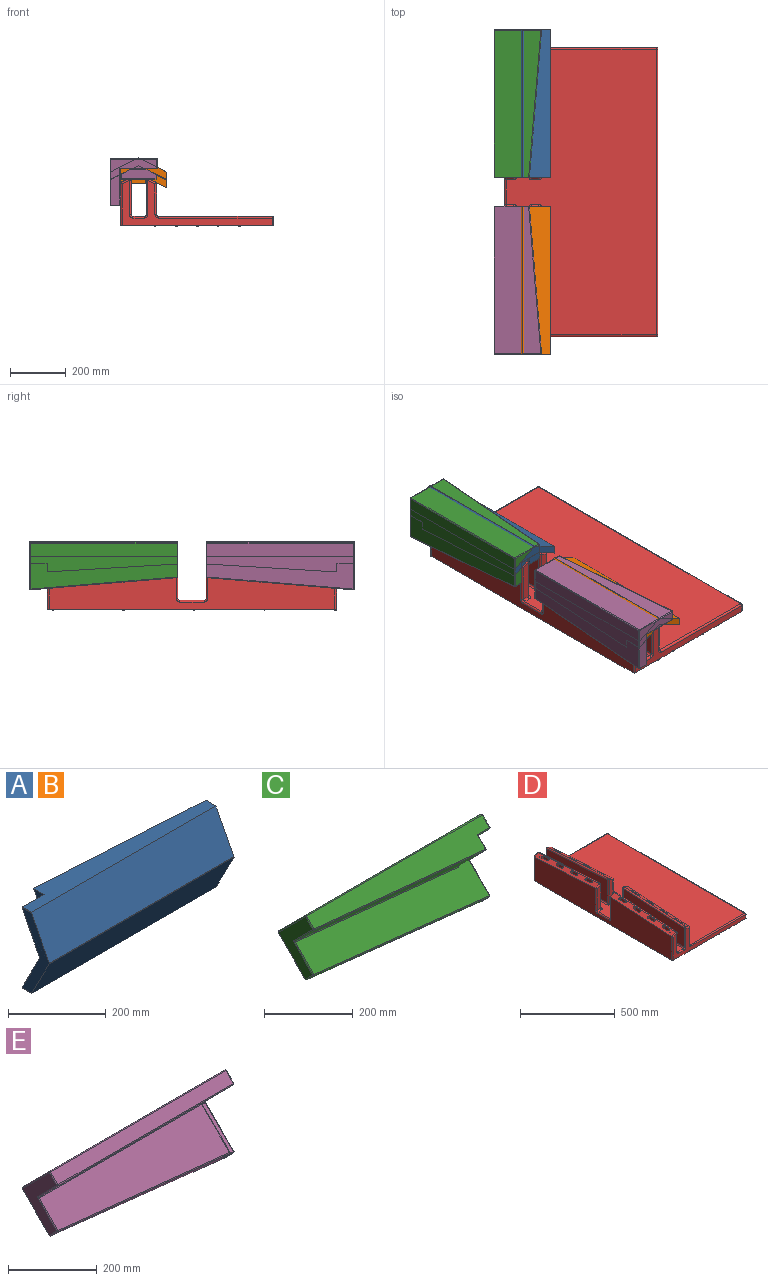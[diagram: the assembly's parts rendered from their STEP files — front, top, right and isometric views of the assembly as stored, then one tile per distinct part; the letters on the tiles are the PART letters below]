
ASSEMBLY  parts=5 mates=8
PART A: 33 faces, bbox 534.4x110.4x204.2 mm
  f0: plane 469.9x75.61mm, normal (0.05,0.89,0.46), area 39897.8mm2, adj f1,f2,f6,f23
  f1: plane 532.14x57.13mm, normal (0,0,-1), area 21788.8mm2, adj f0,f6,f10,f11,f14,f23,f31
  f2: plane 469.9x52.97mm, normal (0,0.02,-1), area 11550.8mm2, adj f0,f6,f15,f23
  f3: plane 469.9x52.97mm, normal (0,0.02,1), area 11550.8mm2, adj f4,f6,f15,f23
  f4: plane 469.9x75.61mm, normal (0.05,0.89,-0.46), area 39897.8mm2, adj f3,f5,f6,f23
  f5: plane 532.14x57.13mm, normal (0,0,1), area 21788.8mm2, adj f4,f6,f8,f9,f16,f23,f32
  f6: plane 203.66x79.94mm, normal (-1,0,0), area 7130.9mm2, adj f0,f1,f2,f3,f4,f5,f9,f10
  f7: sphere r=1.27mm, area 2.2mm2, adj f8,f16,f20
  f8: cylinder r=1.27mm len=60.96mm, axis (-1,0,0), area 158.5mm2, adj f5,f7,f9,f13
  f9: bspline ~2.87x2.62mm, area 4.1mm2, adj f5,f6,f8,f21
  f10: bspline ~2.76x2.54mm, area 4.1mm2, adj f1,f6,f11,f22
  f11: cylinder r=1.27mm len=60.96mm, axis (-1,0,0), area 158.5mm2, adj f1,f10,f12,f18
  f12: sphere r=1.27mm, area 2.2mm2, adj f11,f14,f17
  f13: plane 99.17x62.23mm, normal (0,0.89,-0.46), area 6866mm2, adj f8,f19,f20,f21,f27
  f14: cylinder r=1.27mm len=26.49mm, axis (0,-1,0), area 52.8mm2, adj f1,f12,f19,f29
  f15: plane 469.9x52.11mm, normal (0.06,1,0), area 24298.6mm2, adj f2,f3,f6,f23
  f16: cylinder r=1.27mm len=26.49mm, axis (0,1,0), area 52.8mm2, adj f5,f7,f19,f26
  f17: cylinder r=1.27mm len=54.17mm, axis (0,-0.46,0.89), area 117.8mm2, adj f12,f18,f19,f28
  f18: plane 99.17x62.23mm, normal (0,0.89,0.46), area 6865.9mm2, adj f11,f17,f19,f22,f27,f28
  f19: plane 203.2x78.7mm, normal (-1,0,0), area 5581.4mm2, adj f13,f14,f16,f17,f18,f20,f25,f26
  f20: cylinder r=1.27mm len=54.14mm, axis (0,-0.46,-0.89), area 118.8mm2, adj f7,f13,f19,f25
  f21: cylinder r=1.27mm len=100.91mm, axis (0,0.46,0.89), area 223.5mm2, adj f6,f9,f13,f24
  f22: cylinder r=1.27mm len=100.91mm, axis (0,0.46,-0.89), area 223.5mm2, adj f6,f10,f18,f24
  f23: plane 203.2x80.81mm, normal (1,0,0), area 7457.9mm2, adj f0,f1,f2,f3,f4,f5,f15,f30
  f24: sphere r=1.27mm, area 1.4mm2, adj f21,f22,f27
  f25: plane 3.07x0.99mm, normal (0,1,0), area 0.4mm2, adj f19,f20
  f26: plane 1.27x1.27mm, normal (0,1,0), area 0.3mm2, adj f16,f19,f32
  f27: cylinder r=1.27mm len=62.23mm, axis (-1,0,0), area 75.2mm2, adj f13,f18,f19,f24
  f28: plane 3.81x2.31mm, normal (0,1,0), area 0.8mm2, adj f17,f18,f19
  f29: plane 1.27x1.27mm, normal (0,1,0), area 0.3mm2, adj f14,f19,f31
  f30: cylinder r=1.27mm len=533.4mm, axis (-1,0,0), area 644.7mm2, adj f19,f23,f31,f32
  f31: plane 533.4x101.02mm, normal (0,-0.89,-0.46), area 60618.5mm2, adj f1,f19,f23,f29,f30
  f32: plane 533.4x101.02mm, normal (0,-0.89,0.46), area 60618.5mm2, adj f5,f19,f23,f26,f30
PART B: same geometry as A
PART C: 56 faces, bbox 533.4x170.4x240.4 mm
  f0: cylinder r=2.54mm len=0.77mm, axis (0,-0.71,-0.71), area 0.1mm2, adj f6,f27,f42
  f1: cylinder r=2.54mm len=37.24mm, axis (1,-0.06,0.06), area 138.1mm2, adj f11,f12,f18,f55
  f2: cylinder r=2.54mm len=528.58mm, axis (-1,0.06,0.06), area 2115.4mm2, adj f5,f10,f21,f32
  f3: cylinder r=2.54mm len=528.58mm, axis (1,-0.06,0.06), area 2115.4mm2, adj f7,f12,f22,f31
  f4: cylinder r=2.54mm len=528.37mm, axis (1,0,0), area 2108.1mm2, adj f7,f10,f25,f35
  f5: plane 528.37x54.49mm, normal (-0.08,-0.7,-0.71), area 17507.3mm2, adj f2,f14,f19,f30
  f6: plane 172.76x109.95mm, normal (-1,0,0), area 7001.3mm2, adj f0,f26,f27,f28,f29,f30,f31,f32
  f7: plane 528.37x117.66mm, normal (0,0.71,0.71), area 76157.4mm2, adj f3,f4,f24,f33
  f8: plane 235.02x141.02mm, normal (1,0,0), area 9899.2mm2, adj f15,f16,f17,f18,f19,f20,f21,f22
  f9: plane 528.37x90.7mm, normal (0,-0.71,0.71), area 46551.3mm2, adj f14,f15,f26,f36,f49,f50,f51
  f10: plane 528.37x117.66mm, normal (0,0.71,-0.71), area 76157.4mm2, adj f2,f4,f23,f34
  f11: plane 90.7x90.43mm, normal (0,-0.71,-0.71), area 4049.6mm2, adj f1,f16,f36,f53,f54
  f12: plane 528.37x78.86mm, normal (-0.08,-0.71,0.7), area 26822.7mm2, adj f1,f3,f13,f20,f29,f40,f41,f46
  f13: cylinder r=2.54mm len=0.02mm, axis (1,-0.06,0.06), area 0mm2, adj f12,f27,f40
  f14: cylinder r=2.54mm len=528.58mm, axis (1,-0.06,-0.06), area 2115.4mm2, adj f5,f9,f17,f28
  f15: cylinder r=2.51mm len=96.03mm, axis (0,0.71,0.71), area 515.8mm2, adj f8,f9,f17,f37
  f16: cylinder r=2.51mm len=96.03mm, axis (0,0.71,-0.71), area 515.8mm2, adj f8,f11,f18,f37
  f17: bspline ~3.75x2.72mm, area 10.6mm2, adj f8,f14,f15,f19
  f18: bspline ~3.75x2.72mm, area 10.6mm2, adj f1,f8,f16,f20
  f19: cylinder r=2.51mm len=25.16mm, axis (0,-0.71,0.71), area 137.3mm2, adj f5,f8,f17,f21
  f20: cylinder r=2.51mm len=25.16mm, axis (0,0.71,0.71), area 137.3mm2, adj f8,f12,f18,f22
  f21: bspline ~3.75x2.72mm, area 10.6mm2, adj f2,f8,f19,f23
  f22: bspline ~3.75x2.72mm, area 10.6mm2, adj f3,f8,f20,f24
  f23: cylinder r=2.51mm len=119.43mm, axis (0,-0.71,-0.71), area 656.3mm2, adj f8,f10,f21,f25
  f24: cylinder r=2.51mm len=119.43mm, axis (0,0.71,-0.71), area 656.3mm2, adj f7,f8,f22,f25
  f25: torus R=0.03mm, axis (1,0,0), area 10.1mm2, adj f4,f8,f23,f24
  f26: cylinder r=2.51mm len=64.74mm, axis (0,0.71,0.71), area 338.5mm2, adj f6,f9,f28,f47,f48
  f27: bspline ~3.43x2.5mm, area 0.6mm2, adj f0,f6,f13,f29,f40,f42
  f28: bspline ~3.59x2.51mm, area 9.5mm2, adj f6,f14,f26,f30
  f29: cylinder r=2.51mm len=25.15mm, axis (0,-0.71,-0.71), area 123.5mm2, adj f6,f12,f27,f31
  f30: cylinder r=2.51mm len=25.15mm, axis (0,0.71,-0.71), area 123.5mm2, adj f5,f6,f28,f32
  f31: bspline ~3.59x2.75mm, area 9.5mm2, adj f3,f6,f29,f33
  f32: bspline ~3.59x2.75mm, area 9.5mm2, adj f2,f6,f30,f34
  f33: cylinder r=2.51mm len=88.25mm, axis (0,0.71,-0.71), area 482.4mm2, adj f6,f7,f31,f35
  f34: cylinder r=2.51mm len=88.25mm, axis (0,-0.71,-0.71), area 482.4mm2, adj f6,f10,f32,f35
  f35: torus R=0.03mm, axis (-1,0,0), area 10.1mm2, adj f4,f6,f33,f34
  f36: cylinder r=2.51mm len=31.95mm, axis (-1,0,0), area 126.2mm2, adj f9,f11,f37,f52
  f37: bspline ~5.34x3.56mm, area 6.7mm2, adj f15,f16,f36
  f38: plane 491.32x114.92mm, normal (-0.08,-0.7,-0.71), area 51488.3mm2, adj f41,f43,f44,f48,f49
  f39: plane 111.46x111.27mm, normal (1,0,0), area 4064.3mm2, adj f44,f46,f51,f53
  f40: cylinder r=2.54mm len=0.93mm, axis (0,-0.71,-0.71), area 0.1mm2, adj f12,f13,f27,f42
  f41: cylinder r=2.54mm len=491.41mm, axis (-0.99,0.11,0), area 1964.8mm2, adj f12,f38,f42,f45
  f42: sphere r=2.54mm, area 9mm2, adj f0,f27,f40,f41,f43
  f43: cylinder r=2.54mm len=64.87mm, axis (0,0.71,-0.71), area 328.6mm2, adj f6,f38,f42,f47
  f44: cylinder r=2.54mm len=90.29mm, axis (0,-0.71,0.71), area 522.7mm2, adj f38,f39,f45,f50
  f45: sphere r=2.54mm, area 11.2mm2, adj f41,f44,f46
  f46: cylinder r=2.54mm len=28.42mm, axis (0,-0.71,-0.71), area 144mm2, adj f12,f39,f45,f54,f55
  f47: bspline ~5.36x3.58mm, area 7mm2, adj f26,f43,f48
  f48: bspline ~3.6x0.73mm, area 1mm2, adj f26,f38,f47,f49
  f49: cylinder r=2.54mm len=491.15mm, axis (-1,0.05,0.05), area 1964.5mm2, adj f9,f38,f48,f50
  f50: torus R=5.08mm, axis (0,0.71,-0.71), area 22.8mm2, adj f9,f44,f49,f51
  f51: cylinder r=2.54mm len=24.84mm, axis (0,-0.71,-0.71), area 129.8mm2, adj f9,f39,f50,f52
  f52: bspline ~3.56x2.54mm, area 7.1mm2, adj f36,f51,f53
  f53: cylinder r=2.54mm len=90.3mm, axis (0,0.71,-0.71), area 498.6mm2, adj f11,f39,f52,f54
  f54: torus R=5.08mm, axis (0,-0.71,-0.71), area 1.1mm2, adj f11,f46,f53,f55
  f55: bspline ~5.27x5.24mm, area 6.8mm2, adj f1,f46,f54
PART D: 236 faces, bbox 552.9x1041.8x201.4 mm
  f0: plane 1041.4x552.45mm, normal (0,0,-1), area 560077.8mm2, adj f4,f6,f7,f16,f17,f52,f53,f54
  f1: plane 1028.7x539.75mm, normal (0,0,1), area 468237mm2, adj f14,f15,f24,f25,f28,f32,f33,f39
  f2: plane 151.7x25.4mm, normal (0,1,0), area 3686.9mm2, adj f34,f35,f43,f44
  f3: plane 151.7x25.4mm, normal (0,1,0), area 3686.9mm2, adj f12,f13,f23,f24
  f4: plane 539.75x162.05mm, normal (0,-1,0), area 20422.9mm2, adj f0,f16,f17,f21,f25,f26,f29,f30
  f5: plane 457.2x142.48mm, normal (1,0,0), area 58803.4mm2, adj f11,f26,f33,f34,f35
  f6: plane 1028.7x25.4mm, normal (1,0,0), area 26129mm2, adj f0,f15,f16,f118
  f7: plane 1028.7x180.58mm, normal (-1,0,0), area 155417.8mm2, adj f0,f10,f12,f13,f14,f17,f19,f114
  f8: plane 457.2x151.7mm, normal (-1,0,0), area 63013.9mm2, adj f36,f41,f44,f47
  f9: plane 457.2x151.7mm, normal (1,0,0), area 63013.9mm2, adj f22,f23,f31,f32
  f10: plane 457.65x43.06mm, normal (-0.46,-0.05,0.89), area 12093.9mm2, adj f7,f12,f17,f21,f22,f50,f68,f69
  f11: plane 457.65x43.06mm, normal (0.46,-0.05,0.89), area 12093.9mm2, adj f5,f26,f30,f35,f36,f48,f52,f53
  f12: cylinder r=6.35mm len=31.75mm, axis (0.89,0,0.46), area 320.7mm2, adj f3,f7,f10,f13,f18
  f13: cylinder r=6.35mm len=142.48mm, axis (0,0,1), area 1407.1mm2, adj f3,f7,f12,f19
  f14: cylinder r=6.35mm len=88.9mm, axis (0,1,0), area 886.7mm2, adj f1,f7,f19,f121
  f15: cylinder r=6.35mm len=1028.7mm, axis (0,-1,0), area 10260.8mm2, adj f1,f6,f20,f122
  f16: cylinder r=6.35mm len=25.4mm, axis (0,0,-1), area 253.4mm2, adj f0,f4,f6,f20
  f17: cylinder r=6.35mm len=152.84mm, axis (0,0,1), area 1510.4mm2, adj f0,f4,f7,f10,f21
  f18: sphere r=6.35mm, area 86.1mm2, adj f12,f22,f23
  f19: torus R=12.7mm, axis (-1,0,0), area 135.6mm2, adj f7,f13,f14,f24
  f20: sphere r=6.35mm, area 63.3mm2, adj f15,f16,f25
  f21: cylinder r=6.35mm len=31.74mm, axis (0.89,0,0.46), area 298.5mm2, adj f4,f10,f17,f27
  f22: cylinder r=6.35mm len=457.58mm, axis (0,-1,-0.06), area 5950.7mm2, adj f9,f10,f18,f27
  f23: cylinder r=6.35mm len=151.7mm, axis (0,0,-1), area 1513.1mm2, adj f3,f9,f18,f28
  f24: cylinder r=6.35mm len=25.4mm, axis (-1,0,0), area 253.4mm2, adj f1,f3,f19,f28
  f25: cylinder r=6.35mm len=409.58mm, axis (-1,0,0), area 4085.3mm2, adj f1,f4,f20,f29
  f26: cylinder r=6.35mm len=114.74mm, axis (0,0,-1), area 1130.4mm2, adj f4,f5,f11,f29,f30
  f27: sphere r=6.35mm, area 79mm2, adj f21,f22,f31
  f28: torus R=12.7mm, axis (0,0,-1), area 135.6mm2, adj f1,f23,f24,f32
  f29: torus R=12.7mm, axis (0,1,0), area 135.6mm2, adj f4,f25,f26,f33
  f30: cylinder r=6.35mm len=31.74mm, axis (0.89,0,-0.46), area 298.5mm2, adj f4,f11,f26,f37
  f31: cylinder r=6.35mm len=123.95mm, axis (0,0,-1), area 1236.4mm2, adj f4,f9,f27,f38
  f32: cylinder r=6.35mm len=457.2mm, axis (0,-1,0), area 4560.4mm2, adj f1,f9,f28,f38
  f33: cylinder r=6.35mm len=457.2mm, axis (0,1,0), area 4560.4mm2, adj f1,f5,f29,f39
  f34: cylinder r=6.35mm len=142.48mm, axis (0,0,-1), area 1407.1mm2, adj f2,f5,f35,f39
  f35: cylinder r=6.35mm len=31.75mm, axis (0.89,0,-0.46), area 320.7mm2, adj f2,f5,f11,f34,f40
  f36: cylinder r=6.35mm len=457.58mm, axis (0,1,0.06), area 5950.7mm2, adj f8,f11,f37,f40
  f37: sphere r=6.35mm, area 79mm2, adj f30,f36,f41
  f38: torus R=12.7mm, axis (0,1,0), area 135.6mm2, adj f4,f31,f32,f42
  f39: torus R=12.7mm, axis (0,0,-1), area 135.6mm2, adj f1,f33,f34,f43
  f40: sphere r=6.35mm, area 86.1mm2, adj f35,f36,f44
  f41: cylinder r=6.35mm len=123.95mm, axis (0,0,1), area 1236.4mm2, adj f4,f8,f37,f45
  f42: cylinder r=6.35mm len=41.28mm, axis (1,0,0), area 411.7mm2, adj f1,f4,f38,f45
  f43: cylinder r=6.35mm len=25.4mm, axis (-1,0,0), area 253.4mm2, adj f1,f2,f39,f46
  f44: cylinder r=6.35mm len=151.7mm, axis (0,0,1), area 1513.1mm2, adj f2,f8,f40,f46
  f45: torus R=12.7mm, axis (0,1,0), area 135.6mm2, adj f4,f41,f42,f47
  f46: torus R=12.7mm, axis (0,0,-1), area 135.6mm2, adj f1,f43,f44,f47
  f47: cylinder r=6.35mm len=457.2mm, axis (0,-1,0), area 4560.4mm2, adj f1,f8,f45,f46
  f48: cylinder r=1.9mm len=17.85mm, axis (0,0,1), area 200.7mm2, adj f11,f49
  f49: cone r=0mm half-angle=59deg, axis (0,0,1), area 13.2mm2, adj f48
  f50: cylinder r=1.9mm len=17.85mm, axis (0,0,1), area 200.7mm2, adj f10,f51
  f51: cone r=0mm half-angle=59deg, axis (0,0,1), area 13.2mm2, adj f50
  f52: cylinder r=6.35mm len=167mm, axis (0,0,1), area 3261.2mm2, adj f0,f11,f53,f55
  f53: plane 162.76x38.1mm, normal (-1,0,0), area 6157.2mm2, adj f0,f11,f52,f54
  f54: cylinder r=6.35mm len=169.34mm, axis (0,0,1), area 3317.1mm2, adj f0,f11,f53,f55
  f55: plane 169.31x38.1mm, normal (1,0,0), area 6406.6mm2, adj f0,f11,f52,f54
  f56: cylinder r=6.35mm len=186.65mm, axis (0,0,1), area 3653.3mm2, adj f0,f11,f57,f59
  f57: plane 182.42x38.1mm, normal (-1,0,0), area 6906mm2, adj f0,f11,f56,f58
  f58: cylinder r=6.35mm len=188.99mm, axis (0,0,1), area 3709.2mm2, adj f0,f11,f57,f59
  f59: plane 188.96x38.1mm, normal (1,0,0), area 7155.4mm2, adj f0,f11,f56,f58
  f60: cylinder r=6.35mm len=180.1mm, axis (0,0,1), area 3522.6mm2, adj f0,f11,f61,f63
  f61: plane 175.86x38.1mm, normal (-1,0,0), area 6656.4mm2, adj f0,f11,f60,f62
  f62: cylinder r=6.35mm len=182.44mm, axis (0,0,1), area 3578.5mm2, adj f0,f11,f61,f63
  f63: plane 182.41x38.1mm, normal (1,0,0), area 6905.8mm2, adj f0,f11,f60,f62
  f64: cylinder r=6.35mm len=173.55mm, axis (0,0,1), area 3391.9mm2, adj f0,f11,f65,f67
  f65: plane 169.31x38.1mm, normal (-1,0,0), area 6406.8mm2, adj f0,f11,f64,f66
  f66: cylinder r=6.35mm len=175.89mm, axis (0,0,1), area 3447.8mm2, adj f0,f11,f65,f67
  f67: plane 175.86x38.1mm, normal (1,0,0), area 6656.2mm2, adj f0,f11,f64,f66
  f68: cylinder r=6.35mm len=170.98mm, axis (0,0,1), area 3349.8mm2, adj f0,f10,f69,f71
  f69: plane 164.4x38.1mm, normal (1,0,0), area 6219.5mm2, adj f0,f10,f68,f70
  f70: cylinder r=6.35mm len=168.63mm, axis (0,0,1), area 3293.9mm2, adj f0,f10,f69,f71
  f71: plane 170.94x38.1mm, normal (-1,0,0), area 6468.9mm2, adj f0,f10,f68,f70
  f72: cylinder r=6.35mm len=188.29mm, axis (0,0,1), area 3685.9mm2, adj f0,f10,f73,f75
  f73: plane 190.6x38.1mm, normal (-1,0,0), area 7217.7mm2, adj f0,f10,f72,f74
  f74: cylinder r=6.35mm len=190.63mm, axis (0,0,1), area 3741.9mm2, adj f0,f10,f73,f75
  f75: plane 184.05x38.1mm, normal (1,0,0), area 6968.3mm2, adj f0,f10,f72,f74
  f76: cylinder r=6.35mm len=181.73mm, axis (0,0,1), area 3555.2mm2, adj f0,f10,f77,f79
  f77: plane 184.05x38.1mm, normal (-1,0,0), area 6968.1mm2, adj f0,f10,f76,f78
  f78: cylinder r=6.35mm len=184.08mm, axis (0,0,1), area 3611.2mm2, adj f0,f10,f77,f79
  f79: plane 177.5x38.1mm, normal (1,0,0), area 6718.7mm2, adj f0,f10,f76,f78
  f80: cylinder r=6.35mm len=175.18mm, axis (0,0,1), area 3424.6mm2, adj f0,f10,f81,f83
  f81: plane 177.5x38.1mm, normal (-1,0,0), area 6718.5mm2, adj f0,f10,f80,f82
  f82: cylinder r=6.35mm len=177.53mm, axis (0,0,1), area 3480.5mm2, adj f0,f10,f81,f83
  f83: plane 170.95x38.1mm, normal (1,0,0), area 6469.1mm2, adj f0,f10,f80,f82
  f84: plane 31.75x12.7mm, normal (1,0,0), area 403.2mm2, adj f0,f1,f85,f91
  f85: cylinder r=6.35mm len=31.75mm, axis (0,0,1), area 316.7mm2, adj f0,f1,f84,f86
  f86: plane 31.75x12.7mm, normal (0,1,0), area 403.2mm2, adj f0,f1,f85,f87
  f87: cylinder r=6.35mm len=31.75mm, axis (0,0,1), area 316.7mm2, adj f0,f1,f86,f88
  f88: plane 31.75x12.7mm, normal (-1,0,0), area 403.2mm2, adj f0,f1,f87,f89
  f89: cylinder r=6.35mm len=31.75mm, axis (0,0,1), area 316.7mm2, adj f0,f1,f88,f90
  f90: plane 31.75x12.7mm, normal (0,-1,0), area 403.2mm2, adj f0,f1,f89,f91
  f91: cylinder r=6.35mm len=31.75mm, axis (0,0,1), area 316.7mm2, adj f0,f1,f84,f90
  f92: plane 31.75x12.7mm, normal (1,0,0), area 403.2mm2, adj f0,f1,f93,f99
  f93: cylinder r=6.35mm len=31.75mm, axis (0,0,1), area 316.7mm2, adj f0,f1,f92,f94
  f94: plane 31.75x12.7mm, normal (0,1,0), area 403.2mm2, adj f0,f1,f93,f95
  f95: cylinder r=6.35mm len=31.75mm, axis (0,0,1), area 316.7mm2, adj f0,f1,f94,f96
  f96: plane 31.75x12.7mm, normal (-1,0,0), area 403.2mm2, adj f0,f1,f95,f97
  f97: cylinder r=6.35mm len=31.75mm, axis (0,0,1), area 316.7mm2, adj f0,f1,f96,f98
  f98: plane 31.75x12.7mm, normal (0,-1,0), area 403.2mm2, adj f0,f1,f97,f99
  f99: cylinder r=6.35mm len=31.75mm, axis (0,0,1), area 316.7mm2, adj f0,f1,f92,f98
  f100: plane 31.75x12.7mm, normal (0,-1,0), area 403.2mm2, adj f0,f1,f101,f107
  f101: cylinder r=6.35mm len=31.75mm, axis (0,0,1), area 316.7mm2, adj f0,f1,f100,f102
  f102: plane 31.75x12.7mm, normal (1,0,0), area 403.2mm2, adj f0,f1,f101,f103
  f103: cylinder r=6.35mm len=31.75mm, axis (0,0,1), area 316.7mm2, adj f0,f1,f102,f104
  f104: plane 31.75x12.7mm, normal (0,1,0), area 403.2mm2, adj f0,f1,f103,f105
  f105: cylinder r=6.35mm len=31.75mm, axis (0,0,1), area 316.7mm2, adj f0,f1,f104,f106
  f106: plane 31.75x12.7mm, normal (-1,0,0), area 403.2mm2, adj f0,f1,f105,f107
  f107: cylinder r=6.35mm len=31.75mm, axis (0,0,1), area 316.7mm2, adj f0,f1,f100,f106
  f108: plane 151.7x25.4mm, normal (0,-1,0), area 3686.9mm2, adj f136,f137,f145,f146
  f109: plane 151.7x25.4mm, normal (0,-1,0), area 3686.9mm2, adj f116,f117,f125,f126
  f110: plane 539.75x162.05mm, normal (0,1,0), area 20422.9mm2, adj f0,f118,f119,f123,f127,f128,f131,f132
  f111: plane 457.2x142.48mm, normal (1,0,0), area 58803.4mm2, adj f115,f128,f135,f136,f137
  f112: plane 457.2x151.7mm, normal (-1,0,0), area 63013.9mm2, adj f138,f143,f146,f149
  f113: plane 457.2x151.7mm, normal (1,0,0), area 63013.9mm2, adj f124,f125,f133,f134
  f114: plane 457.65x43.06mm, normal (-0.46,0.05,0.89), area 12093.9mm2, adj f7,f116,f119,f123,f124,f152,f170,f171
  f115: plane 457.65x43.06mm, normal (0.46,0.05,0.89), area 12093.9mm2, adj f111,f128,f132,f137,f138,f150,f154,f155
  f116: cylinder r=6.35mm len=31.75mm, axis (0.89,0,0.46), area 320.7mm2, adj f7,f109,f114,f117,f120
  f117: cylinder r=6.35mm len=142.48mm, axis (0,0,1), area 1407.1mm2, adj f7,f109,f116,f121
  f118: cylinder r=6.35mm len=25.4mm, axis (0,0,-1), area 253.4mm2, adj f0,f6,f110,f122
  f119: cylinder r=6.35mm len=152.84mm, axis (0,0,1), area 1510.4mm2, adj f0,f7,f110,f114,f123
  f120: sphere r=6.35mm, area 86.1mm2, adj f116,f124,f125
  f121: torus R=12.7mm, axis (-1,0,0), area 135.6mm2, adj f7,f14,f117,f126
  f122: sphere r=6.35mm, area 63.3mm2, adj f15,f118,f127
  f123: cylinder r=6.35mm len=31.74mm, axis (0.89,0,0.46), area 298.5mm2, adj f110,f114,f119,f129
  f124: cylinder r=6.35mm len=457.58mm, axis (0,1,-0.06), area 5950.7mm2, adj f113,f114,f120,f129
  f125: cylinder r=6.35mm len=151.7mm, axis (0,0,-1), area 1513.1mm2, adj f109,f113,f120,f130
  f126: cylinder r=6.35mm len=25.4mm, axis (-1,0,0), area 253.4mm2, adj f1,f109,f121,f130
  f127: cylinder r=6.35mm len=409.58mm, axis (-1,0,0), area 4085.3mm2, adj f1,f110,f122,f131
  f128: cylinder r=6.35mm len=114.74mm, axis (0,0,-1), area 1130.4mm2, adj f110,f111,f115,f131,f132
  f129: sphere r=6.35mm, area 79mm2, adj f123,f124,f133
  f130: torus R=12.7mm, axis (0,0,-1), area 135.6mm2, adj f1,f125,f126,f134
  f131: torus R=12.7mm, axis (0,-1,0), area 135.6mm2, adj f110,f127,f128,f135
  f132: cylinder r=6.35mm len=31.74mm, axis (0.89,0,-0.46), area 298.5mm2, adj f110,f115,f128,f139
  f133: cylinder r=6.35mm len=123.95mm, axis (0,0,-1), area 1236.4mm2, adj f110,f113,f129,f140
  f134: cylinder r=6.35mm len=457.2mm, axis (0,1,0), area 4560.4mm2, adj f1,f113,f130,f140
  f135: cylinder r=6.35mm len=457.2mm, axis (0,-1,0), area 4560.4mm2, adj f1,f111,f131,f141
  f136: cylinder r=6.35mm len=142.48mm, axis (0,0,-1), area 1407.1mm2, adj f108,f111,f137,f141
  f137: cylinder r=6.35mm len=31.75mm, axis (0.89,0,-0.46), area 320.7mm2, adj f108,f111,f115,f136,f142
  f138: cylinder r=6.35mm len=457.58mm, axis (0,-1,0.06), area 5950.7mm2, adj f112,f115,f139,f142
  f139: sphere r=6.35mm, area 79mm2, adj f132,f138,f143
  f140: torus R=12.7mm, axis (0,-1,0), area 135.6mm2, adj f110,f133,f134,f144
  f141: torus R=12.7mm, axis (0,0,-1), area 135.6mm2, adj f1,f135,f136,f145
  f142: sphere r=6.35mm, area 86.1mm2, adj f137,f138,f146
  f143: cylinder r=6.35mm len=123.95mm, axis (0,0,1), area 1236.4mm2, adj f110,f112,f139,f147
  f144: cylinder r=6.35mm len=41.28mm, axis (1,0,0), area 411.7mm2, adj f1,f110,f140,f147
  f145: cylinder r=6.35mm len=25.4mm, axis (-1,0,0), area 253.4mm2, adj f1,f108,f141,f148
  f146: cylinder r=6.35mm len=151.7mm, axis (0,0,1), area 1513.1mm2, adj f108,f112,f142,f148
  f147: torus R=12.7mm, axis (0,-1,0), area 135.6mm2, adj f110,f143,f144,f149
  f148: torus R=12.7mm, axis (0,0,-1), area 135.6mm2, adj f1,f145,f146,f149
  f149: cylinder r=6.35mm len=457.2mm, axis (0,1,0), area 4560.4mm2, adj f1,f112,f147,f148
  f150: cylinder r=1.9mm len=17.85mm, axis (0,0,1), area 200.7mm2, adj f115,f151
  f151: cone r=0mm half-angle=59deg, axis (0,0,1), area 13.2mm2, adj f150
  f152: cylinder r=1.9mm len=17.85mm, axis (0,0,1), area 200.7mm2, adj f114,f153
  f153: cone r=0mm half-angle=59deg, axis (0,0,1), area 13.2mm2, adj f152
  f154: cylinder r=6.35mm len=167mm, axis (0,0,1), area 3261.2mm2, adj f0,f115,f155,f157
  f155: plane 162.76x38.1mm, normal (-1,0,0), area 6157.2mm2, adj f0,f115,f154,f156
  f156: cylinder r=6.35mm len=169.34mm, axis (0,0,1), area 3317.1mm2, adj f0,f115,f155,f157
  f157: plane 169.31x38.1mm, normal (1,0,0), area 6406.6mm2, adj f0,f115,f154,f156
  f158: cylinder r=6.35mm len=186.65mm, axis (0,0,1), area 3653.3mm2, adj f0,f115,f159,f161
  f159: plane 182.42x38.1mm, normal (-1,0,0), area 6906mm2, adj f0,f115,f158,f160
  f160: cylinder r=6.35mm len=188.99mm, axis (0,0,1), area 3709.2mm2, adj f0,f115,f159,f161
  f161: plane 188.96x38.1mm, normal (1,0,0), area 7155.4mm2, adj f0,f115,f158,f160
  f162: cylinder r=6.35mm len=180.1mm, axis (0,0,1), area 3522.6mm2, adj f0,f115,f163,f165
  f163: plane 175.86x38.1mm, normal (-1,0,0), area 6656.4mm2, adj f0,f115,f162,f164,f225
  f164: cylinder r=6.35mm len=182.44mm, axis (0,0,1), area 3578.5mm2, adj f0,f115,f163,f165
  f165: plane 182.41x38.1mm, normal (1,0,0), area 6905.8mm2, adj f0,f115,f162,f164
  f166: cylinder r=6.35mm len=173.55mm, axis (0,0,1), area 3391.9mm2, adj f0,f115,f167,f169
  f167: plane 169.31x38.1mm, normal (-1,0,0), area 6406.8mm2, adj f0,f115,f166,f168
  f168: cylinder r=6.35mm len=175.89mm, axis (0,0,1), area 3447.8mm2, adj f0,f115,f167,f169
  f169: plane 175.86x38.1mm, normal (1,0,0), area 6656.2mm2, adj f0,f115,f166,f168
  f170: cylinder r=6.35mm len=170.98mm, axis (0,0,1), area 3349.8mm2, adj f0,f114,f171,f173
  f171: plane 164.4x38.1mm, normal (1,0,0), area 6219.5mm2, adj f0,f114,f170,f172
  f172: cylinder r=6.35mm len=168.63mm, axis (0,0,1), area 3293.9mm2, adj f0,f114,f171,f173
  f173: plane 170.94x38.1mm, normal (-1,0,0), area 6468.9mm2, adj f0,f114,f170,f172
  f174: cylinder r=6.35mm len=188.29mm, axis (0,0,1), area 3685.9mm2, adj f0,f114,f175,f177
  f175: plane 190.6x38.1mm, normal (-1,0,0), area 7217.7mm2, adj f0,f114,f174,f176
  f176: cylinder r=6.35mm len=190.63mm, axis (0,0,1), area 3741.9mm2, adj f0,f114,f175,f177
  f177: plane 184.05x38.1mm, normal (1,0,0), area 6968.3mm2, adj f0,f114,f174,f176
  f178: cylinder r=6.35mm len=181.73mm, axis (0,0,1), area 3555.2mm2, adj f0,f114,f179,f181
  f179: plane 184.05x38.1mm, normal (-1,0,0), area 6968.1mm2, adj f0,f114,f178,f180
  f180: cylinder r=6.35mm len=184.08mm, axis (0,0,1), area 3611.2mm2, adj f0,f114,f179,f181
  f181: plane 177.5x38.1mm, normal (1,0,0), area 6718.7mm2, adj f0,f114,f178,f180
  f182: cylinder r=6.35mm len=175.18mm, axis (0,0,1), area 3424.6mm2, adj f0,f114,f183,f185
  f183: plane 177.5x38.1mm, normal (-1,0,0), area 6718.5mm2, adj f0,f114,f182,f184
  f184: cylinder r=6.35mm len=177.53mm, axis (0,0,1), area 3480.5mm2, adj f0,f114,f183,f185
  f185: plane 170.95x38.1mm, normal (1,0,0), area 6469.1mm2, adj f0,f114,f182,f184
  f186: plane 31.75x12.7mm, normal (1,0,0), area 403.2mm2, adj f0,f1,f187,f193
  f187: cylinder r=6.35mm len=31.75mm, axis (0,0,1), area 316.7mm2, adj f0,f1,f186,f188
  f188: plane 31.75x12.7mm, normal (0,-1,0), area 403.2mm2, adj f0,f1,f187,f189
  f189: cylinder r=6.35mm len=31.75mm, axis (0,0,1), area 316.7mm2, adj f0,f1,f188,f190
  f190: plane 31.75x12.7mm, normal (-1,0,0), area 403.2mm2, adj f0,f1,f189,f191
  f191: cylinder r=6.35mm len=31.75mm, axis (0,0,1), area 316.7mm2, adj f0,f1,f190,f192
  f192: plane 31.75x12.7mm, normal (0,1,0), area 403.2mm2, adj f0,f1,f191,f193
  f193: cylinder r=6.35mm len=31.75mm, axis (0,0,1), area 316.7mm2, adj f0,f1,f186,f192
  f194: plane 31.75x12.7mm, normal (1,0,0), area 403.2mm2, adj f0,f1,f195,f201
  f195: cylinder r=6.35mm len=31.75mm, axis (0,0,1), area 316.7mm2, adj f0,f1,f194,f196
  f196: plane 31.75x12.7mm, normal (0,-1,0), area 403.2mm2, adj f0,f1,f195,f197
  f197: cylinder r=6.35mm len=31.75mm, axis (0,0,1), area 316.7mm2, adj f0,f1,f196,f198
  f198: plane 31.75x12.7mm, normal (-1,0,0), area 403.2mm2, adj f0,f1,f197,f199
  f199: cylinder r=6.35mm len=31.75mm, axis (0,0,1), area 316.7mm2, adj f0,f1,f198,f200
  f200: plane 31.75x12.7mm, normal (0,1,0), area 403.2mm2, adj f0,f1,f199,f201
  f201: cylinder r=6.35mm len=31.75mm, axis (0,0,1), area 316.7mm2, adj f0,f1,f194,f200
  f202: plane 31.75x12.7mm, normal (0,1,0), area 403.2mm2, adj f0,f1,f203,f209
  f203: cylinder r=6.35mm len=31.75mm, axis (0,0,1), area 316.7mm2, adj f0,f1,f202,f204
  f204: plane 31.75x12.7mm, normal (1,0,0), area 403.2mm2, adj f0,f1,f203,f205
  f205: cylinder r=6.35mm len=31.75mm, axis (0,0,1), area 316.7mm2, adj f0,f1,f204,f206
  f206: plane 31.75x12.7mm, normal (0,-1,0), area 403.2mm2, adj f0,f1,f205,f207
  f207: cylinder r=6.35mm len=31.75mm, axis (0,0,1), area 316.7mm2, adj f0,f1,f206,f208
  f208: plane 31.75x12.7mm, normal (-1,0,0), area 403.2mm2, adj f0,f1,f207,f209
  f209: cylinder r=6.35mm len=31.75mm, axis (0,0,1), area 316.7mm2, adj f0,f1,f202,f208
  f210: sphere r=4.76mm, area 142.5mm2, adj f0
  f211: sphere r=4.76mm, area 142.5mm2, adj f0
  f212: sphere r=4.76mm, area 142.5mm2, adj f0
  f213: sphere r=4.76mm, area 142.5mm2, adj f0
  f214: sphere r=4.76mm, area 142.5mm2, adj f0
  f215: sphere r=4.76mm, area 142.5mm2, adj f0
  f216: sphere r=4.76mm, area 142.5mm2, adj f0
  f217: sphere r=4.76mm, area 142.5mm2, adj f0
  f218: sphere r=4.76mm, area 142.5mm2, adj f0
  f219: sphere r=4.76mm, area 142.5mm2, adj f0
  f220: sphere r=4.76mm, area 142.5mm2, adj f0
  f221: sphere r=4.76mm, area 142.5mm2, adj f0
  f222: sphere r=4.76mm, area 142.5mm2, adj f0
  f223: sphere r=4.76mm, area 142.5mm2, adj f0
  f224: sphere r=4.76mm, area 142.5mm2, adj f0
  f225: plane 6.04x1.08mm, normal (0,0,1), area 4.5mm2, adj f163,f226
  f226: sphere r=4.76mm, area 142.5mm2, adj f0,f225
  f227: sphere r=4.76mm, area 142.5mm2, adj f0
  f228: sphere r=4.76mm, area 142.5mm2, adj f0
  f229: sphere r=4.76mm, area 142.5mm2, adj f0
  f230: sphere r=4.76mm, area 142.5mm2, adj f0
  f231: sphere r=4.76mm, area 142.5mm2, adj f0
  f232: sphere r=4.76mm, area 142.5mm2, adj f0
  f233: sphere r=4.76mm, area 142.5mm2, adj f0
  f234: sphere r=4.76mm, area 142.5mm2, adj f0
  f235: sphere r=4.76mm, area 142.5mm2, adj f0
PART E: 56 faces, bbox 533.4x170.4x240.4 mm
  f0: cylinder r=2.54mm len=0.77mm, axis (0,-0.71,0.71), area 0.1mm2, adj f6,f27,f42
  f1: cylinder r=2.54mm len=37.24mm, axis (1,-0.06,-0.06), area 138.1mm2, adj f11,f12,f18,f55
  f2: cylinder r=2.54mm len=528.58mm, axis (-1,0.06,-0.06), area 2115.4mm2, adj f5,f10,f21,f32
  f3: cylinder r=2.54mm len=528.58mm, axis (1,-0.06,-0.06), area 2115.4mm2, adj f7,f12,f22,f31
  f4: cylinder r=2.54mm len=528.37mm, axis (1,0,0), area 2108.1mm2, adj f7,f10,f25,f35
  f5: plane 528.37x54.49mm, normal (-0.08,-0.7,0.71), area 17507.3mm2, adj f2,f14,f19,f30
  f6: plane 172.76x109.95mm, normal (-1,0,0), area 7001.3mm2, adj f0,f26,f27,f28,f29,f30,f31,f32
  f7: plane 528.37x117.66mm, normal (0,0.71,-0.71), area 76157.4mm2, adj f3,f4,f24,f33
  f8: plane 235.02x141.02mm, normal (1,0,0), area 9899.2mm2, adj f15,f16,f17,f18,f19,f20,f21,f22
  f9: plane 528.37x90.7mm, normal (0,-0.71,-0.71), area 46551.3mm2, adj f14,f15,f26,f36,f49,f50,f51
  f10: plane 528.37x117.66mm, normal (0,0.71,0.71), area 76157.4mm2, adj f2,f4,f23,f34
  f11: plane 90.7x90.43mm, normal (0,-0.71,0.71), area 4049.6mm2, adj f1,f16,f36,f53,f54
  f12: plane 528.37x78.86mm, normal (-0.08,-0.71,-0.7), area 26822.7mm2, adj f1,f3,f13,f20,f29,f40,f41,f46
  f13: cylinder r=2.54mm len=0.02mm, axis (1,-0.06,-0.06), area 0mm2, adj f12,f27,f40
  f14: cylinder r=2.54mm len=528.58mm, axis (1,-0.06,0.06), area 2115.4mm2, adj f5,f9,f17,f28
  f15: cylinder r=2.51mm len=96.03mm, axis (0,0.71,-0.71), area 515.8mm2, adj f8,f9,f17,f37
  f16: cylinder r=2.51mm len=96.03mm, axis (0,0.71,0.71), area 515.8mm2, adj f8,f11,f18,f37
  f17: bspline ~3.75x2.72mm, area 10.6mm2, adj f8,f14,f15,f19
  f18: bspline ~3.75x2.72mm, area 10.6mm2, adj f1,f8,f16,f20
  f19: cylinder r=2.51mm len=25.16mm, axis (0,-0.71,-0.71), area 137.3mm2, adj f5,f8,f17,f21
  f20: cylinder r=2.51mm len=25.16mm, axis (0,0.71,-0.71), area 137.3mm2, adj f8,f12,f18,f22
  f21: bspline ~3.75x2.72mm, area 10.6mm2, adj f2,f8,f19,f23
  f22: bspline ~3.75x2.72mm, area 10.6mm2, adj f3,f8,f20,f24
  f23: cylinder r=2.51mm len=119.43mm, axis (0,-0.71,0.71), area 656.3mm2, adj f8,f10,f21,f25
  f24: cylinder r=2.51mm len=119.43mm, axis (0,0.71,0.71), area 656.3mm2, adj f7,f8,f22,f25
  f25: torus R=0.03mm, axis (1,0,0), area 10.1mm2, adj f4,f8,f23,f24
  f26: cylinder r=2.51mm len=64.74mm, axis (0,0.71,-0.71), area 338.4mm2, adj f6,f9,f28,f47,f48
  f27: bspline ~3.43x2.5mm, area 0.6mm2, adj f0,f6,f13,f29,f40,f42
  f28: bspline ~3.59x2.51mm, area 9.5mm2, adj f6,f14,f26,f30
  f29: cylinder r=2.51mm len=25.15mm, axis (0,-0.71,0.71), area 123.5mm2, adj f6,f12,f27,f31
  f30: cylinder r=2.51mm len=25.15mm, axis (0,0.71,0.71), area 123.5mm2, adj f5,f6,f28,f32
  f31: bspline ~3.59x2.75mm, area 9.5mm2, adj f3,f6,f29,f33
  f32: bspline ~3.59x2.75mm, area 9.5mm2, adj f2,f6,f30,f34
  f33: cylinder r=2.51mm len=88.25mm, axis (0,0.71,0.71), area 482.4mm2, adj f6,f7,f31,f35
  f34: cylinder r=2.51mm len=88.25mm, axis (0,-0.71,0.71), area 482.4mm2, adj f6,f10,f32,f35
  f35: torus R=0.03mm, axis (-1,0,0), area 10.1mm2, adj f4,f6,f33,f34
  f36: cylinder r=2.51mm len=31.95mm, axis (-1,0,0), area 126.2mm2, adj f9,f11,f37,f52
  f37: bspline ~5.34x3.56mm, area 6.7mm2, adj f15,f16,f36
  f38: plane 491.32x114.92mm, normal (-0.08,-0.7,0.71), area 51488.3mm2, adj f41,f43,f44,f48,f49
  f39: plane 111.46x111.27mm, normal (1,0,0), area 4064.3mm2, adj f44,f46,f51,f53
  f40: cylinder r=2.54mm len=0.93mm, axis (0,-0.71,0.71), area 0.1mm2, adj f12,f13,f27,f42
  f41: cylinder r=2.54mm len=491.41mm, axis (-0.99,0.11,0), area 1964.8mm2, adj f12,f38,f42,f45
  f42: sphere r=2.54mm, area 9mm2, adj f0,f27,f40,f41,f43
  f43: cylinder r=2.54mm len=64.87mm, axis (0,0.71,0.71), area 328.6mm2, adj f6,f38,f42,f47
  f44: cylinder r=2.54mm len=90.29mm, axis (0,-0.71,-0.71), area 522.7mm2, adj f38,f39,f45,f50
  f45: sphere r=2.54mm, area 11.2mm2, adj f41,f44,f46
  f46: cylinder r=2.54mm len=28.42mm, axis (0,-0.71,0.71), area 144mm2, adj f12,f39,f45,f54,f55
  f47: bspline ~5.36x3.58mm, area 7mm2, adj f26,f43,f48
  f48: bspline ~3.6x0.73mm, area 1mm2, adj f26,f38,f47,f49
  f49: cylinder r=2.54mm len=491.15mm, axis (-1,0.05,-0.05), area 1964.5mm2, adj f9,f38,f48,f50
  f50: torus R=5.08mm, axis (0,0.71,0.71), area 22.8mm2, adj f9,f44,f49,f51
  f51: cylinder r=2.54mm len=24.84mm, axis (0,-0.71,0.71), area 129.8mm2, adj f9,f39,f50,f52
  f52: bspline ~3.56x2.54mm, area 7.1mm2, adj f36,f51,f53
  f53: cylinder r=2.54mm len=90.3mm, axis (0,0.71,0.71), area 498.6mm2, adj f11,f39,f52,f54
  f54: torus R=5.08mm, axis (0,-0.71,0.71), area 1.1mm2, adj f11,f46,f53,f55
  f55: bspline ~5.27x5.24mm, area 6.8mm2, adj f1,f46,f54
PLACE A rot(axis=(-0.58,0.58,-0.58),120deg) t=(509.46,2209.06,-197.42)mm
PLACE B rot(axis=(-0.58,-0.58,0.58),120deg) t=(-381.18,-1180.36,-197.52)mm
PLACE C rot(axis=(0.36,0.36,0.86),98.4deg) t=(175.99,1098.55,453.79)mm
PLACE D t=(65.09,-69.85,241.69)mm
PLACE E rot(axis=(0.68,-0.68,-0.28),148.7deg) t=(-35.63,-69.85,241.55)mm
MATE planar A.f4 <-> D.f115  axis (-0.46,-0.05,-0.89) through (127.96,800.36,167.84)mm
MATE planar C.f9 <-> D.f7  axis (1,0,0) through (0,840.47,137.94)mm
MATE planar E.f7 <-> C.f7  axis (0,0,1) through (25.5,461.04,240.73)mm
MATE planar D.f2 <-> E.f6  axis (0,1,0) through (110.93,463.55,110.73)mm
MATE planar E.f9 <-> D.f7  axis (1,0,0) through (0,-67.34,136.07)mm
MATE planar D.f108 <-> A.f23  axis (0,-1,0) through (111.12,565.15,183.25)mm
MATE planar B.f0 <-> D.f11  axis (-0.46,0.05,-0.89) through (128.16,228.34,167.74)mm
MATE planar B.f23 <-> D.f2  axis (0,1,0) through (128.28,463.55,181.95)mm
